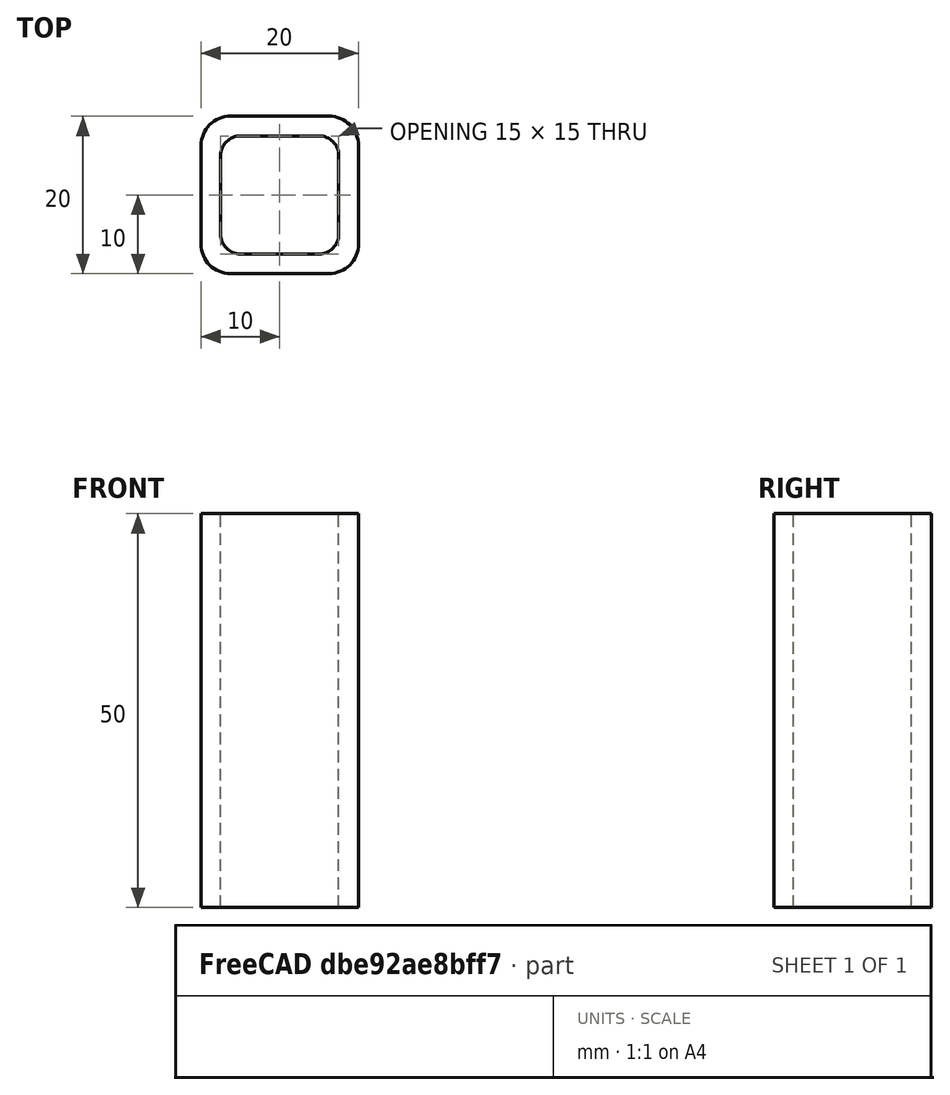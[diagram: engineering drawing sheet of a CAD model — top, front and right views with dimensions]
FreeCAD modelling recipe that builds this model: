
FCSTD DOCUMENT  (FreeCAD 0.15R4671 (Git))
Label: Square hollow section 20x20x2.5 EN10219 S235JRH
License: All rights reserved
LicenseURL: http://en.wikipedia.org/wiki/All_rights_reserved
objects: Sketcher::SketchObject×1, Part::Extrusion×1
note: 2 computed .brp shape members not serialized (recipe doc carries the construction recipe); baked Part::Feature solids carry a one-line shape summary decoded from their .brp

FEATURE [Sketcher::SketchObject] Sketch
  sketch-geometry (16):
    g0: LineSegment StartX=-5 StartY=7.5 StartZ=0 EndX=5 EndY=7.5 EndZ=0
    g1: LineSegment StartX=7.5 StartY=5 StartZ=0 EndX=7.5 EndY=-5 EndZ=0
    g2: LineSegment StartX=5 StartY=-7.5 StartZ=0 EndX=-5 EndY=-7.5 EndZ=0
    g3: LineSegment StartX=-7.5 StartY=-5 StartZ=0 EndX=-7.5 EndY=5 EndZ=0
    g4: LineSegment StartX=-6.25 StartY=10 StartZ=0 EndX=6.25 EndY=10 EndZ=0
    g5: LineSegment StartX=10 StartY=6.25 StartZ=0 EndX=10 EndY=-6.25 EndZ=0
    g6: LineSegment StartX=6.25 StartY=-10 StartZ=0 EndX=-6.25 EndY=-10 EndZ=0
    g7: LineSegment StartX=-10 StartY=-6.25 StartZ=0 EndX=-10 EndY=6.25 EndZ=0
    g8: ArcOfCircle CenterX=-5 CenterY=5 CenterZ=0 NormalX=0 NormalY=0 NormalZ=1 Radius=2.5 StartAngle=1.5708 EndAngle=3.14159
    g9: ArcOfCircle CenterX=5 CenterY=5 CenterZ=0 NormalX=0 NormalY=0 NormalZ=1 Radius=2.5 StartAngle=0 EndAngle=1.5708
    g10: ArcOfCircle CenterX=5 CenterY=-5 CenterZ=0 NormalX=0 NormalY=0 NormalZ=1 Radius=2.5 StartAngle=4.71239 EndAngle=6.28319
    g11: ArcOfCircle CenterX=-5 CenterY=-5 CenterZ=0 NormalX=0 NormalY=0 NormalZ=1 Radius=2.5 StartAngle=3.14159 EndAngle=4.71239
    g12: ArcOfCircle CenterX=6.25 CenterY=6.25 CenterZ=0 NormalX=0 NormalY=0 NormalZ=1 Radius=3.75 StartAngle=0 EndAngle=1.5708
    g13: ArcOfCircle CenterX=6.25 CenterY=-6.25 CenterZ=0 NormalX=0 NormalY=0 NormalZ=1 Radius=3.75 StartAngle=4.71239 EndAngle=6.28319
    g14: ArcOfCircle CenterX=-6.25 CenterY=-6.25 CenterZ=0 NormalX=0 NormalY=0 NormalZ=1 Radius=3.75 StartAngle=3.14159 EndAngle=4.71239
    g15: ArcOfCircle CenterX=-6.25 CenterY=6.25 CenterZ=0 NormalX=0 NormalY=0 NormalZ=1 Radius=3.75 StartAngle=1.5708 EndAngle=3.14159
  constraints (36):
    c: Horizontal(g2)
    c: Vertical(g3)
    c: Horizontal(g6)
    c: Vertical(g7)
    c: Tangent(g3,g8) = 1.5708
    c: Tangent(g0,g8) = 1.5708
    c: Tangent(g0,g9) = 1.5708
    c: Tangent(g1,g9) = 1.5708
    c: Tangent(g1,g10) = 1.5708
    c: Tangent(g2,g10) = 1.5708
    c: Tangent(g2,g11) = 1.5708
    c: Tangent(g3,g11) = 1.5708
    c: Tangent(g4,g12) = 1.5708
    c: Tangent(g5,g12) = 1.5708
    c: Tangent(g5,g13) = 1.5708
    c: Tangent(g6,g13) = 1.5708
    c: Tangent(g6,g14) = 1.5708
    c: Tangent(g7,g14) = 1.5708
    c: Tangent(g7,g15) = 1.5708
    c: Tangent(g4,g15) = 1.5708
    c: Equal(g9,g8)
    c: Equal(g9,g11)
    c: Equal(g9,g10)
    c: Equal(g12,g15)
    c: Equal(g12,g14)
    c: Equal(g12,g13)
    c: Symmetric(g4,g6,g-1)
    c: Symmetric(g7,g5,g-2)
    c: DistanceY(g4,g6) = -20
    c: DistanceX(g7,g5) = 20
    c: Symmetric(g3,g1,g-2)
    c: Symmetric(g0,g2,g-1)
    c: DistanceY(g0,g4) = 2.5
    c: DistanceX(g5,g1) = -2.5
    c: Radius(g9) = 2.5
    c: Radius(g12) = 3.75
FEATURE [Part::Extrusion] Extrude  label="Square hollow section 20x20x2.5 EN10219 S235JRH"
  Base = -> Sketch
  Dir = (0,0,50)
  Solid = true
